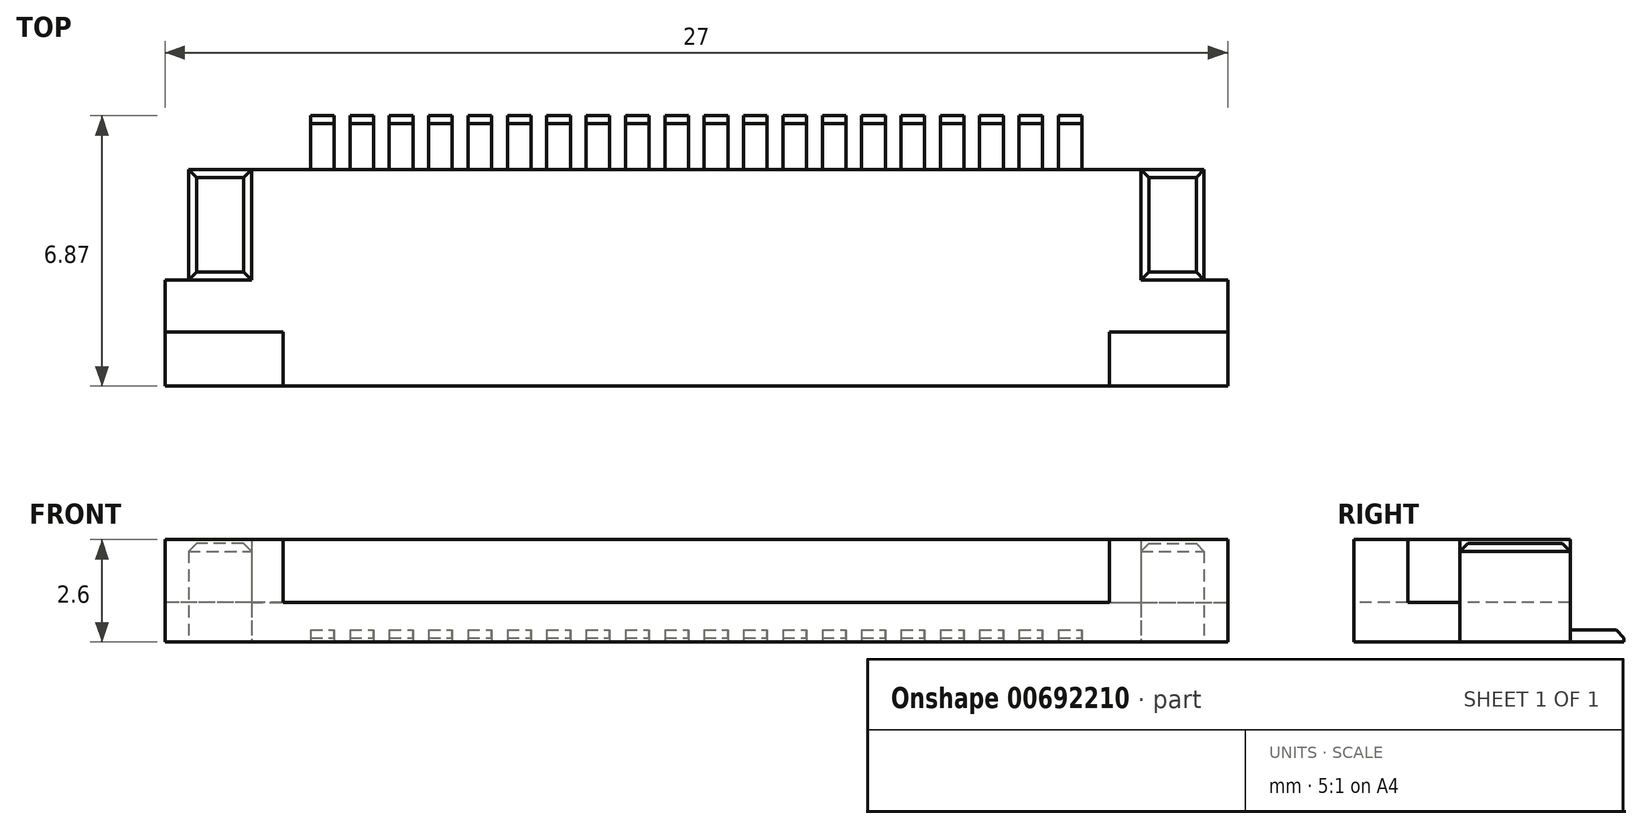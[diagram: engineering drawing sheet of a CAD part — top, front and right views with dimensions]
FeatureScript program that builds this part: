
annotation { "Feature Type Name" : "Feature", "Feature Type Description" : "" }
export const myFeature = defineFeature(function(context is Context, id is Id, definition is map)
    precondition{}
    {
        {
            var Q0;
            Q0=qCreatedBy(makeId("Top.planeOp"),FACE);
            var sketch = newSketch(context, id + "F0", { "sketchPlane" : qUnion([Q0])});
            skLineSegment(sketch, "E0.bottom", {"start": v(-12.9, 2.75) * mm, "end": v(12.9, 2.75) * mm});
            skLineSegment(sketch, "E0.top", {"start": v(-13.5, -2.75) * mm, "end": v(13.5, -2.75) * mm});
            skLineSegment(sketch, "E0.left", {"start": v(-13.5, -0.05) * mm, "end": v(-13.5, -2.75) * mm});
            skLineSegment(sketch, "E0.right", {"start": v(13.5, -0.05) * mm, "end": v(13.5, -2.75) * mm});
            skPoint(sketch, "E0.middle", {"position": v(0, 0) * mm});
            skLineSegment(sketch, "E1", {"start": v(-10.5, -1.37) * mm, "end": v(-10.5, -2.75) * mm});
            skLineSegment(sketch, "E2", {"start": v(10.5, -1.37) * mm, "end": v(10.5, -2.75) * mm});
            skLineSegment(sketch, "E3", {"start": v(-0.2, 2.75) * mm, "end": v(-0.2, 4.12) * mm});
            skLineSegment(sketch, "E4", {"start": v(-0.2, 4.12) * mm, "end": v(-0.8, 4.12) * mm});
            skLineSegment(sketch, "E5", {"start": v(-0.8, 4.12) * mm, "end": v(-0.8, 2.75) * mm});
            skLineSegment(sketch, "E6.1.0.0", {"start": v(-1.8, 4.12) * mm, "end": v(-1.8, 2.75) * mm});
            skLineSegment(sketch, "E6.1.0.1", {"start": v(-1.2, 4.12) * mm, "end": v(-1.8, 4.12) * mm});
            skLineSegment(sketch, "E6.1.0.2", {"start": v(-1.2, 2.75) * mm, "end": v(-1.2, 4.12) * mm});
            skLineSegment(sketch, "E6.2.0.0", {"start": v(-2.8, 4.12) * mm, "end": v(-2.8, 2.75) * mm});
            skLineSegment(sketch, "E6.2.0.1", {"start": v(-2.2, 4.12) * mm, "end": v(-2.8, 4.12) * mm});
            skLineSegment(sketch, "E6.2.0.2", {"start": v(-2.2, 2.75) * mm, "end": v(-2.2, 4.12) * mm});
            skLineSegment(sketch, "E6.3.0.0", {"start": v(-3.8, 4.12) * mm, "end": v(-3.8, 2.75) * mm});
            skLineSegment(sketch, "E6.3.0.1", {"start": v(-3.2, 4.12) * mm, "end": v(-3.8, 4.12) * mm});
            skLineSegment(sketch, "E6.3.0.2", {"start": v(-3.2, 2.75) * mm, "end": v(-3.2, 4.12) * mm});
            skLineSegment(sketch, "E6.4.0.0", {"start": v(-4.8, 4.12) * mm, "end": v(-4.8, 2.75) * mm});
            skLineSegment(sketch, "E6.4.0.1", {"start": v(-4.2, 4.12) * mm, "end": v(-4.8, 4.12) * mm});
            skLineSegment(sketch, "E6.4.0.2", {"start": v(-4.2, 2.75) * mm, "end": v(-4.2, 4.12) * mm});
            skLineSegment(sketch, "E6.5.0.0", {"start": v(-5.8, 4.12) * mm, "end": v(-5.8, 2.75) * mm});
            skLineSegment(sketch, "E6.5.0.1", {"start": v(-5.2, 4.12) * mm, "end": v(-5.8, 4.12) * mm});
            skLineSegment(sketch, "E6.5.0.2", {"start": v(-5.2, 2.75) * mm, "end": v(-5.2, 4.12) * mm});
            skLineSegment(sketch, "E6.6.0.0", {"start": v(-6.8, 4.12) * mm, "end": v(-6.8, 2.75) * mm});
            skLineSegment(sketch, "E6.6.0.1", {"start": v(-6.2, 4.12) * mm, "end": v(-6.8, 4.12) * mm});
            skLineSegment(sketch, "E6.6.0.2", {"start": v(-6.2, 2.75) * mm, "end": v(-6.2, 4.12) * mm});
            skLineSegment(sketch, "E6.7.0.0", {"start": v(-7.8, 4.12) * mm, "end": v(-7.8, 2.75) * mm});
            skLineSegment(sketch, "E6.7.0.1", {"start": v(-7.2, 4.12) * mm, "end": v(-7.8, 4.12) * mm});
            skLineSegment(sketch, "E6.7.0.2", {"start": v(-7.2, 2.75) * mm, "end": v(-7.2, 4.12) * mm});
            skLineSegment(sketch, "E6.8.0.0", {"start": v(-8.8, 4.12) * mm, "end": v(-8.8, 2.75) * mm});
            skLineSegment(sketch, "E6.8.0.1", {"start": v(-8.2, 4.12) * mm, "end": v(-8.8, 4.12) * mm});
            skLineSegment(sketch, "E6.8.0.2", {"start": v(-8.2, 2.75) * mm, "end": v(-8.2, 4.12) * mm});
            skLineSegment(sketch, "E6.direction1", {"start": v(-0.8, 2.75) * mm, "end": v(-1.8, 2.75) * mm, "construction": true});
            skLineSegment(sketch, "E7.0.9.0", {"start": v(-9.8, 4.12) * mm, "end": v(-9.8, 2.75) * mm});
            skLineSegment(sketch, "E7.3.9.0", {"start": v(-9.2, 4.12) * mm, "end": v(-9.8, 4.12) * mm});
            skLineSegment(sketch, "E7.6.9.0", {"start": v(-9.2, 2.75) * mm, "end": v(-9.2, 4.12) * mm});
            skLineSegment(sketch, "E8.1.0.0", {"start": v(0.2, 4.12) * mm, "end": v(0.2, 2.75) * mm});
            skLineSegment(sketch, "E8.1.0.1", {"start": v(0.8, 4.12) * mm, "end": v(0.2, 4.12) * mm});
            skLineSegment(sketch, "E8.1.0.2", {"start": v(0.8, 2.75) * mm, "end": v(0.8, 4.12) * mm});
            skLineSegment(sketch, "E8.2.0.0", {"start": v(1.2, 4.12) * mm, "end": v(1.2, 2.75) * mm});
            skLineSegment(sketch, "E8.2.0.1", {"start": v(1.8, 4.12) * mm, "end": v(1.2, 4.12) * mm});
            skLineSegment(sketch, "E8.2.0.2", {"start": v(1.8, 2.75) * mm, "end": v(1.8, 4.12) * mm});
            skLineSegment(sketch, "E8.3.0.0", {"start": v(2.2, 4.12) * mm, "end": v(2.2, 2.75) * mm});
            skLineSegment(sketch, "E8.3.0.1", {"start": v(2.8, 4.12) * mm, "end": v(2.2, 4.12) * mm});
            skLineSegment(sketch, "E8.3.0.2", {"start": v(2.8, 2.75) * mm, "end": v(2.8, 4.12) * mm});
            skLineSegment(sketch, "E8.4.0.0", {"start": v(3.2, 4.12) * mm, "end": v(3.2, 2.75) * mm});
            skLineSegment(sketch, "E8.4.0.1", {"start": v(3.8, 4.12) * mm, "end": v(3.2, 4.12) * mm});
            skLineSegment(sketch, "E8.4.0.2", {"start": v(3.8, 2.75) * mm, "end": v(3.8, 4.12) * mm});
            skLineSegment(sketch, "E8.5.0.0", {"start": v(4.2, 4.12) * mm, "end": v(4.2, 2.75) * mm});
            skLineSegment(sketch, "E8.5.0.1", {"start": v(4.8, 4.12) * mm, "end": v(4.2, 4.12) * mm});
            skLineSegment(sketch, "E8.5.0.2", {"start": v(4.8, 2.75) * mm, "end": v(4.8, 4.12) * mm});
            skLineSegment(sketch, "E8.6.0.0", {"start": v(5.2, 4.12) * mm, "end": v(5.2, 2.75) * mm});
            skLineSegment(sketch, "E8.6.0.1", {"start": v(5.8, 4.12) * mm, "end": v(5.2, 4.12) * mm});
            skLineSegment(sketch, "E8.6.0.2", {"start": v(5.8, 2.75) * mm, "end": v(5.8, 4.12) * mm});
            skLineSegment(sketch, "E8.7.0.0", {"start": v(6.2, 4.12) * mm, "end": v(6.2, 2.75) * mm});
            skLineSegment(sketch, "E8.7.0.1", {"start": v(6.8, 4.12) * mm, "end": v(6.2, 4.12) * mm});
            skLineSegment(sketch, "E8.7.0.2", {"start": v(6.8, 2.75) * mm, "end": v(6.8, 4.12) * mm});
            skLineSegment(sketch, "E8.8.0.0", {"start": v(7.2, 4.12) * mm, "end": v(7.2, 2.75) * mm});
            skLineSegment(sketch, "E8.8.0.1", {"start": v(7.8, 4.12) * mm, "end": v(7.2, 4.12) * mm});
            skLineSegment(sketch, "E8.8.0.2", {"start": v(7.8, 2.75) * mm, "end": v(7.8, 4.12) * mm});
            skLineSegment(sketch, "E8.9.0.0", {"start": v(8.2, 4.12) * mm, "end": v(8.2, 2.75) * mm});
            skLineSegment(sketch, "E8.9.0.1", {"start": v(8.8, 4.12) * mm, "end": v(8.2, 4.12) * mm});
            skLineSegment(sketch, "E8.9.0.2", {"start": v(8.8, 2.75) * mm, "end": v(8.8, 4.12) * mm});
            skLineSegment(sketch, "E8.10.0.0", {"start": v(9.2, 4.12) * mm, "end": v(9.2, 2.75) * mm});
            skLineSegment(sketch, "E8.10.0.1", {"start": v(9.8, 4.12) * mm, "end": v(9.2, 4.12) * mm});
            skLineSegment(sketch, "E8.10.0.2", {"start": v(9.8, 2.75) * mm, "end": v(9.8, 4.12) * mm});
            skLineSegment(sketch, "E8.direction1", {"start": v(-0.8, 2.75) * mm, "end": v(0.2, 2.75) * mm, "construction": true});
            skLineSegment(sketch, "E9", {"start": v(-10.5, -2.25) * mm, "end": v(10.5, -2.25) * mm});
            skLineSegment(sketch, "E10", {"start": v(-10.5, -1.37) * mm, "end": v(-13.5, -1.37) * mm});
            skLineSegment(sketch, "E11", {"start": v(10.5, -1.37) * mm, "end": v(13.5, -1.37) * mm});
            skLineSegment(sketch, "E12", {"start": v(-12.9, 2.75) * mm, "end": v(-12.9, -0.05) * mm});
            skLineSegment(sketch, "E13", {"start": v(12.9, -0.05) * mm, "end": v(12.9, 2.75) * mm});
            skLineSegment(sketch, "E14", {"start": v(-11.3, 2.75) * mm, "end": v(-11.3, -0.05) * mm});
            skLineSegment(sketch, "E15", {"start": v(-11.3, -0.05) * mm, "end": v(-12.9, -0.05) * mm});
            skLineSegment(sketch, "E16.MirrorCS", {"start": v(11.3, 2.75) * mm, "end": v(11.3, -0.05) * mm});
            skLineSegment(sketch, "E17.MirrorCS", {"start": v(11.3, -0.05) * mm, "end": v(12.9, -0.05) * mm});
            skPoint(sketch, "E18.orphan", {"position": v(-10.5, 0) * mm});
            skPoint(sketch, "E19.orphan", {"position": v(10.5, 0) * mm});
            skLineSegment(sketch, "E20", {"start": v(-12.9, -0.05) * mm, "end": v(-13.5, -0.05) * mm});
            skLineSegment(sketch, "E21", {"start": v(12.9, -0.05) * mm, "end": v(13.5, -0.05) * mm});
            skSolve(sketch);
        }
        {
            var Q0;
            {var subQ33=sQuery(id+"F0.wireOp",EDGE,"E9");Q0=makeQuery(id+"F0.imprint","IMPRINT",FACE,{"disambiguationData":[TD([[makeQuery(id+"F0.imprint","IMPRINT",EDGE,{"derivedFrom":subQ33}),1.0]])]});}
            extrude(context, id + "F1", {"entities" : qUnion([Q0]), "depth" : 1 * mm, "offsetDistance" : 25 * mm});
        }
        {
            var Q0;
            {var subQ4=sQuery(id+"F0.wireOp",EDGE,"E10");Q0=makeQuery(id+"F0.imprint","IMPRINT",FACE,{"disambiguationData":[TD([[makeQuery(id+"F0.imprint","IMPRINT",EDGE,{"derivedFrom":subQ4}),1.0]])]});}
            var Q1;
            {var subQ4=sQuery(id+"F0.wireOp",EDGE,"E11");Q1=makeQuery(id+"F0.imprint","IMPRINT",FACE,{"disambiguationData":[TD([[makeQuery(id+"F0.imprint","IMPRINT",EDGE,{"derivedFrom":subQ4}),-1.0]])]});}
            extrude(context, id + "F2", {"entities" : qUnion([Q0, Q1]), "depth" : 2.6 * mm, "offsetDistance" : 25 * mm});
        }
        {
            var Q0;
            {var subQ5=sQuery(id+"F0.wireOp",EDGE,"E9");Q0=makeQuery(id+"F0.imprint","IMPRINT",FACE,{"disambiguationData":[TD([[makeQuery(id+"F0.imprint","IMPRINT",EDGE,{"derivedFrom":subQ5}),-1.0]])]});}
            extrude(context, id + "F3", {"entities" : qUnion([Q0]), "operationType" : NewBodyOperationType.ADD, "depth" : 1 * mm, "offsetDistance" : 25 * mm});
        }
        {
            var Q0;
            Q0=qCreatedBy(makeId("Top.planeOp"),FACE);
            cPlane(context, id + "F4", {"entities" : qUnion([Q0]), "cplaneType" : CPlaneType.OFFSET, "offset" : 1 * mm, "width" : 150 * mm, "height" : 150 * mm});
        }
        {
            var Q0;
            Q0=makeQuery(id+"F1.opExtrude","CAP_FACE",FACE,{"disambiguationData":[OSD([sQuery(id+"F0.wireOp",EDGE,"E0.bottom"),sQuery(id+"F0.wireOp",EDGE,"E0.left"),sQuery(id+"F0.wireOp",EDGE,"E0.right"),sQuery(id+"F0.wireOp",EDGE,"E1"),sQuery(id+"F0.wireOp",EDGE,"E2"),sQuery(id+"F0.wireOp",EDGE,"E9"),sQuery(id+"F0.wireOp",EDGE,"E10"),sQuery(id+"F0.wireOp",EDGE,"E11"),sQuery(id+"F0.wireOp",EDGE,"E14"),sQuery(id+"F0.wireOp",EDGE,"E15"),sQuery(id+"F0.wireOp",EDGE,"E16.MirrorCS"),sQuery(id+"F0.wireOp",EDGE,"E17.MirrorCS"),sQuery(id+"F0.wireOp",EDGE,"E20"),sQuery(id+"F0.wireOp",EDGE,"E21")])],"isStart":false});
            extrude(context, id + "F5", {"entities" : qUnion([Q0]), "depth" : 1.6 * mm, "offsetDistance" : 25 * mm});
        }
        {
            var Q0;
            {var subQ0=sQuery(id+"F0.wireOp",EDGE,"E12");Q0=makeQuery(id+"F0.imprint","IMPRINT",FACE,{"disambiguationData":[TD([[makeQuery(id+"F0.imprint","IMPRINT",EDGE,{"derivedFrom":subQ0}),1.0]])]});}
            var Q1;
            {var subQ0=sQuery(id+"F0.wireOp",EDGE,"E13");Q1=makeQuery(id+"F0.imprint","IMPRINT",FACE,{"disambiguationData":[TD([[makeQuery(id+"F0.imprint","IMPRINT",EDGE,{"derivedFrom":subQ0}),1.0]])]});}
            extrude(context, id + "F6", {"entities" : qUnion([Q0, Q1]), "depth" : 2.5 * mm, "offsetDistance" : 25 * mm});
        }
        {
            var Q0;
            {var subQ0=sQuery(id+"F0.wireOp",EDGE,"E7.0.9.0");Q0=makeQuery(id+"F0.imprint","IMPRINT",FACE,{"disambiguationData":[TD([[makeQuery(id+"F0.imprint","IMPRINT",EDGE,{"derivedFrom":subQ0}),1.0]])]});}
            var Q1;
            {var subQ0=sQuery(id+"F0.wireOp",EDGE,"E6.8.0.0");Q1=makeQuery(id+"F0.imprint","IMPRINT",FACE,{"disambiguationData":[TD([[makeQuery(id+"F0.imprint","IMPRINT",EDGE,{"derivedFrom":subQ0}),1.0]])]});}
            var Q2;
            {var subQ0=sQuery(id+"F0.wireOp",EDGE,"E6.7.0.0");Q2=makeQuery(id+"F0.imprint","IMPRINT",FACE,{"disambiguationData":[TD([[makeQuery(id+"F0.imprint","IMPRINT",EDGE,{"derivedFrom":subQ0}),1.0]])]});}
            var Q3;
            {var subQ0=sQuery(id+"F0.wireOp",EDGE,"E6.6.0.0");Q3=makeQuery(id+"F0.imprint","IMPRINT",FACE,{"disambiguationData":[TD([[makeQuery(id+"F0.imprint","IMPRINT",EDGE,{"derivedFrom":subQ0}),1.0]])]});}
            var Q4;
            {var subQ0=sQuery(id+"F0.wireOp",EDGE,"E6.5.0.0");Q4=makeQuery(id+"F0.imprint","IMPRINT",FACE,{"disambiguationData":[TD([[makeQuery(id+"F0.imprint","IMPRINT",EDGE,{"derivedFrom":subQ0}),1.0]])]});}
            var Q5;
            {var subQ0=sQuery(id+"F0.wireOp",EDGE,"E6.4.0.0");Q5=makeQuery(id+"F0.imprint","IMPRINT",FACE,{"disambiguationData":[TD([[makeQuery(id+"F0.imprint","IMPRINT",EDGE,{"derivedFrom":subQ0}),1.0]])]});}
            var Q6;
            {var subQ0=sQuery(id+"F0.wireOp",EDGE,"E6.3.0.0");Q6=makeQuery(id+"F0.imprint","IMPRINT",FACE,{"disambiguationData":[TD([[makeQuery(id+"F0.imprint","IMPRINT",EDGE,{"derivedFrom":subQ0}),1.0]])]});}
            var Q7;
            {var subQ0=sQuery(id+"F0.wireOp",EDGE,"E6.2.0.0");Q7=makeQuery(id+"F0.imprint","IMPRINT",FACE,{"disambiguationData":[TD([[makeQuery(id+"F0.imprint","IMPRINT",EDGE,{"derivedFrom":subQ0}),1.0]])]});}
            var Q8;
            {var subQ0=sQuery(id+"F0.wireOp",EDGE,"E6.1.0.0");Q8=makeQuery(id+"F0.imprint","IMPRINT",FACE,{"disambiguationData":[TD([[makeQuery(id+"F0.imprint","IMPRINT",EDGE,{"derivedFrom":subQ0}),1.0]])]});}
            var Q9;
            {var subQ0=sQuery(id+"F0.wireOp",EDGE,"E3");Q9=makeQuery(id+"F0.imprint","IMPRINT",FACE,{"disambiguationData":[TD([[makeQuery(id+"F0.imprint","IMPRINT",EDGE,{"derivedFrom":subQ0}),1.0]])]});}
            var Q10;
            {var subQ0=sQuery(id+"F0.wireOp",EDGE,"E8.1.0.0");Q10=makeQuery(id+"F0.imprint","IMPRINT",FACE,{"disambiguationData":[TD([[makeQuery(id+"F0.imprint","IMPRINT",EDGE,{"derivedFrom":subQ0}),1.0]])]});}
            var Q11;
            {var subQ0=sQuery(id+"F0.wireOp",EDGE,"E8.2.0.0");Q11=makeQuery(id+"F0.imprint","IMPRINT",FACE,{"disambiguationData":[TD([[makeQuery(id+"F0.imprint","IMPRINT",EDGE,{"derivedFrom":subQ0}),1.0]])]});}
            var Q12;
            {var subQ0=sQuery(id+"F0.wireOp",EDGE,"E8.3.0.0");Q12=makeQuery(id+"F0.imprint","IMPRINT",FACE,{"disambiguationData":[TD([[makeQuery(id+"F0.imprint","IMPRINT",EDGE,{"derivedFrom":subQ0}),1.0]])]});}
            var Q13;
            {var subQ0=sQuery(id+"F0.wireOp",EDGE,"E8.4.0.0");Q13=makeQuery(id+"F0.imprint","IMPRINT",FACE,{"disambiguationData":[TD([[makeQuery(id+"F0.imprint","IMPRINT",EDGE,{"derivedFrom":subQ0}),1.0]])]});}
            var Q14;
            {var subQ0=sQuery(id+"F0.wireOp",EDGE,"E8.5.0.0");Q14=makeQuery(id+"F0.imprint","IMPRINT",FACE,{"disambiguationData":[TD([[makeQuery(id+"F0.imprint","IMPRINT",EDGE,{"derivedFrom":subQ0}),1.0]])]});}
            var Q15;
            {var subQ0=sQuery(id+"F0.wireOp",EDGE,"E8.6.0.0");Q15=makeQuery(id+"F0.imprint","IMPRINT",FACE,{"disambiguationData":[TD([[makeQuery(id+"F0.imprint","IMPRINT",EDGE,{"derivedFrom":subQ0}),1.0]])]});}
            var Q16;
            {var subQ0=sQuery(id+"F0.wireOp",EDGE,"E8.7.0.0");Q16=makeQuery(id+"F0.imprint","IMPRINT",FACE,{"disambiguationData":[TD([[makeQuery(id+"F0.imprint","IMPRINT",EDGE,{"derivedFrom":subQ0}),1.0]])]});}
            var Q17;
            {var subQ0=sQuery(id+"F0.wireOp",EDGE,"E8.8.0.0");Q17=makeQuery(id+"F0.imprint","IMPRINT",FACE,{"disambiguationData":[TD([[makeQuery(id+"F0.imprint","IMPRINT",EDGE,{"derivedFrom":subQ0}),1.0]])]});}
            var Q18;
            {var subQ0=sQuery(id+"F0.wireOp",EDGE,"E8.9.0.0");Q18=makeQuery(id+"F0.imprint","IMPRINT",FACE,{"disambiguationData":[TD([[makeQuery(id+"F0.imprint","IMPRINT",EDGE,{"derivedFrom":subQ0}),1.0]])]});}
            var Q19;
            {var subQ0=sQuery(id+"F0.wireOp",EDGE,"E8.10.0.0");Q19=makeQuery(id+"F0.imprint","IMPRINT",FACE,{"disambiguationData":[TD([[makeQuery(id+"F0.imprint","IMPRINT",EDGE,{"derivedFrom":subQ0}),1.0]])]});}
            extrude(context, id + "F7", {"entities" : qUnion([Q0, Q1, Q2, Q3, Q4, Q5, Q6, Q7, Q8, Q9, Q10, Q11, Q12, Q13, Q14, Q15, Q16, Q17, Q18, Q19]), "depth" : 0.3 * mm, "offsetDistance" : 25 * mm});
        }
        {
            var Q0;
            Q0=makeQuery(id+"F7.opExtrude","CAP_EDGE",EDGE,{"disambiguationData":[OSD([sQuery(id+"F0.wireOp",EDGE,"E8.10.0.1")])],"isStart":false});
            var Q1;
            Q1=makeQuery(id+"F7.opExtrude","CAP_EDGE",EDGE,{"disambiguationData":[OSD([sQuery(id+"F0.wireOp",EDGE,"E8.9.0.1")])],"isStart":false});
            var Q2;
            Q2=makeQuery(id+"F7.opExtrude","CAP_EDGE",EDGE,{"disambiguationData":[OSD([sQuery(id+"F0.wireOp",EDGE,"E8.8.0.1")])],"isStart":false});
            var Q3;
            Q3=makeQuery(id+"F7.opExtrude","CAP_EDGE",EDGE,{"disambiguationData":[OSD([sQuery(id+"F0.wireOp",EDGE,"E8.7.0.1")])],"isStart":false});
            var Q4;
            Q4=makeQuery(id+"F7.opExtrude","CAP_EDGE",EDGE,{"disambiguationData":[OSD([sQuery(id+"F0.wireOp",EDGE,"E8.6.0.1")])],"isStart":false});
            var Q5;
            Q5=makeQuery(id+"F7.opExtrude","CAP_EDGE",EDGE,{"disambiguationData":[OSD([sQuery(id+"F0.wireOp",EDGE,"E8.5.0.1")])],"isStart":false});
            var Q6;
            Q6=makeQuery(id+"F7.opExtrude","CAP_EDGE",EDGE,{"disambiguationData":[OSD([sQuery(id+"F0.wireOp",EDGE,"E8.4.0.1")])],"isStart":false});
            var Q7;
            Q7=makeQuery(id+"F7.opExtrude","CAP_EDGE",EDGE,{"disambiguationData":[OSD([sQuery(id+"F0.wireOp",EDGE,"E8.3.0.1")])],"isStart":false});
            var Q8;
            Q8=makeQuery(id+"F7.opExtrude","CAP_EDGE",EDGE,{"disambiguationData":[OSD([sQuery(id+"F0.wireOp",EDGE,"E8.2.0.1")])],"isStart":false});
            var Q9;
            Q9=makeQuery(id+"F7.opExtrude","CAP_EDGE",EDGE,{"disambiguationData":[OSD([sQuery(id+"F0.wireOp",EDGE,"E8.1.0.1")])],"isStart":false});
            var Q10;
            Q10=makeQuery(id+"F7.opExtrude","CAP_EDGE",EDGE,{"disambiguationData":[OSD([sQuery(id+"F0.wireOp",EDGE,"E4")])],"isStart":false});
            var Q11;
            Q11=makeQuery(id+"F7.opExtrude","CAP_EDGE",EDGE,{"disambiguationData":[OSD([sQuery(id+"F0.wireOp",EDGE,"E6.1.0.1")])],"isStart":false});
            var Q12;
            Q12=makeQuery(id+"F7.opExtrude","CAP_EDGE",EDGE,{"disambiguationData":[OSD([sQuery(id+"F0.wireOp",EDGE,"E6.2.0.1")])],"isStart":false});
            var Q13;
            Q13=makeQuery(id+"F7.opExtrude","CAP_EDGE",EDGE,{"disambiguationData":[OSD([sQuery(id+"F0.wireOp",EDGE,"E6.3.0.1")])],"isStart":false});
            var Q14;
            Q14=makeQuery(id+"F7.opExtrude","CAP_EDGE",EDGE,{"disambiguationData":[OSD([sQuery(id+"F0.wireOp",EDGE,"E6.4.0.1")])],"isStart":false});
            var Q15;
            Q15=makeQuery(id+"F7.opExtrude","CAP_EDGE",EDGE,{"disambiguationData":[OSD([sQuery(id+"F0.wireOp",EDGE,"E6.5.0.1")])],"isStart":false});
            var Q16;
            Q16=makeQuery(id+"F7.opExtrude","CAP_EDGE",EDGE,{"disambiguationData":[OSD([sQuery(id+"F0.wireOp",EDGE,"E6.6.0.1")])],"isStart":false});
            var Q17;
            Q17=makeQuery(id+"F7.opExtrude","CAP_EDGE",EDGE,{"disambiguationData":[OSD([sQuery(id+"F0.wireOp",EDGE,"E6.7.0.1")])],"isStart":false});
            var Q18;
            Q18=makeQuery(id+"F7.opExtrude","CAP_EDGE",EDGE,{"disambiguationData":[OSD([sQuery(id+"F0.wireOp",EDGE,"E6.8.0.1")])],"isStart":false});
            var Q19;
            Q19=makeQuery(id+"F7.opExtrude","CAP_EDGE",EDGE,{"disambiguationData":[OSD([sQuery(id+"F0.wireOp",EDGE,"E7.3.9.0")])],"isStart":false});
            chamfer(context, id + "F8", {"entities" : qUnion([Q0, Q1, Q2, Q3, Q4, Q5, Q6, Q7, Q8, Q9, Q10, Q11, Q12, Q13, Q14, Q15, Q16, Q17, Q18, Q19]), "width" : 0.2 * mm, "tangentPropagation" : true});
        }
        {
            var Q0;
            {var subQ0=sQuery(id+"F0.wireOp",EDGE,"E0.bottom");Q0=makeQuery(id+"F6.opExtrude","CAP_EDGE",EDGE,{"disambiguationData":[OSD([subQ0]),TDD([makeQuery(id+"F0.imprint","IMPRINT",EDGE,{"disambiguationData":[TD([[makeQuery(id+"F0.imprint","INTERSECT",VERTEX,{"derivedFrom":[subQ0,sQuery(id+"F0.wireOp",EDGE,"E13")]}),1.0]])],"derivedFrom":subQ0})])],"isStart":false});}
            var Q1;
            Q1=makeQuery(id+"F6.opExtrude","CAP_EDGE",EDGE,{"disambiguationData":[OSD([sQuery(id+"F0.wireOp",EDGE,"E13")])],"isStart":false});
            var Q2;
            {var subQ0=sQuery(id+"F0.wireOp",EDGE,"E0.bottom");Q2=makeQuery(id+"F6.opExtrude","CAP_EDGE",EDGE,{"disambiguationData":[OSD([subQ0]),TDD([makeQuery(id+"F0.imprint","IMPRINT",EDGE,{"disambiguationData":[TD([[makeQuery(id+"F0.imprint","INTERSECT",VERTEX,{"derivedFrom":[subQ0,sQuery(id+"F0.wireOp",EDGE,"E12")]}),-1.0]])],"derivedFrom":subQ0})])],"isStart":false});}
            var Q3;
            Q3=makeQuery(id+"F6.opExtrude","CAP_EDGE",EDGE,{"disambiguationData":[OSD([sQuery(id+"F0.wireOp",EDGE,"E12")])],"isStart":false});
            var Q4;
            Q4=makeQuery(id+"F6.opExtrude","CAP_EDGE",EDGE,{"disambiguationData":[OSD([sQuery(id+"F0.wireOp",EDGE,"E14")])],"isStart":false});
            var Q5;
            Q5=makeQuery(id+"F6.opExtrude","CAP_EDGE",EDGE,{"disambiguationData":[OSD([sQuery(id+"F0.wireOp",EDGE,"E15")])],"isStart":false});
            var Q6;
            Q6=makeQuery(id+"F6.opExtrude","CAP_FACE",FACE,{"disambiguationData":[OSD([sQuery(id+"F0.wireOp",EDGE,"E0.bottom"),sQuery(id+"F0.wireOp",EDGE,"E13"),sQuery(id+"F0.wireOp",EDGE,"E16.MirrorCS"),sQuery(id+"F0.wireOp",EDGE,"E17.MirrorCS")])],"isStart":false});
            chamfer(context, id + "F9", {"entities" : qUnion([Q0, Q1, Q2, Q3, Q4, Q5, Q6]), "width" : 0.2 * mm, "tangentPropagation" : true});
        }
    });
